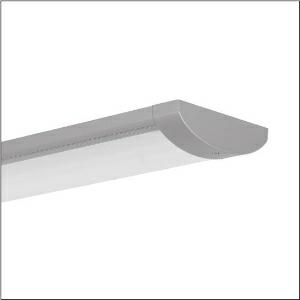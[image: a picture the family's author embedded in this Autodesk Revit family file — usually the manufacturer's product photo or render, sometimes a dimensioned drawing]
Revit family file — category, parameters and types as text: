
# Revit family: tv_20_5xa861d2n0a
name_source: partatom
category: Lighting Fixtures
units: mm (PartAtom-declared; Revit-internal decimal feet)

## family parameters
Cut with Voids When Loaded = No
Host = Face
Light Source = No
Part Type = Normal
Room Calculation Point = No
Round Connector Dimension = Use Diameter
Shared = No

## types (1)
- TV 20 (1 x LED 4000K / CRI = 80 (unbekannt), 2130 lm, 4000K)
    Apparent Load = 21 VA
    CIE Flux Codes = 48 78 95 99 100
    Color Rendering = 80
    Color Temperature = 4000K
    Default Elevation = 1800 mm
    Description = TV 20, vandal-proof luminaire, primary light control with specular reflector, of aluminium, matt, primary optical cover: enclosure, of PC, frosted, light emission: direct distribution, primary light characteristic: symmetric, installation type: surface-mounted, LED, rated luminous flux: 2.130lm, luminous efficacy: 101lm/W, light colour: 840, colour temperature: 4000K, control gear: DALI, mains connection: 230V, AC, 50Hz, rated input power: 21W, luminaire housing, of aluminium, coated, Siteco® metallic grey (DB 702S), with wall and ceiling fixing element, length: 705mm, width: 260mm, height: 70mm, mounting height: 2.5..4.0m, protection rating (complete): IP65, insulation class (complete): insulation class I (protective earthing), certification: CE, protection symbol: F, impact resistance: 2x IK10, standard: EN 60598, packaging unit: 1 piece
    Height = 70 mm
    Lamp = 1 x LED 4000K / CRI >= 80 (unbekannt)
    Lamp Light Flux = 2130 lm
    Lamp count = 1
    Length = 705 mm
    Luminous efficacy = 101 lm/W
    Manufacturer = Siteco
    ModVariant = No
    Model = 5XA861D2N0A
    Mounting Place = Ceiling
    Mounting Type = Surface mounted
    Number of Poles = 1
    OnlyDefault = Yes
    Power Factor = 1
    Product Name = TV 20
    Product group = vandal-proof luminaire
    ProductGroupID = 309
    Protection Class = Protection class I
    Protection Degree = IP 65
    RLX_Detail_Level = 1
    RLX_Emergency_Light_Flux = 0 lm
    RLX_Emergency_Type = 0
    RLX_Emergency_Type_DB = No
    RlxData = <blob elided: 34193 chars, md5=f32839bc>
    Socket = socket
    Standby Power = 0 W
    System Light Flux = 2130 lm
    System Power = 21 W
    Type Comments = Product without accessories
    Type Image = l_1004809.jpg
    URL = http://relux.com
    VarID = ---
    Voltage = 0 V
    Weight = 0.00 kg
    Width = 260 mm

## geometry (parser evidence)
native form markers: Blend x4, Sweep x10
no freeform markers — native parametric forms only
